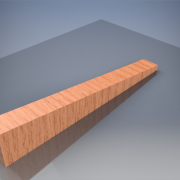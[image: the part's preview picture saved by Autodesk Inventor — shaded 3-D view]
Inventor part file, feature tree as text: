
AUTODESK INVENTOR PART (.ipt)
format: ipt  version: 2018 (Build 220112000, 112)  size: 120,320 bytes
history: native  units: in
note: dims shown in document units (in); Inventor stores cm internally (conversion verified against a paired STEP export)
features: extrude x1, sketch x1
ambient origin geometry x8: Origin, YZ Plane, XZ Plane, XY Plane, X Axis, Y Axis, Z Axis, Center Point
bodies: Solid1 (feature_tree)
feature tree (2):
  extrude  "Extrusion1"  Depth=7.5in
  sketch  "Sketch1"  dims[d0=1.25in d1=7.5in d2=0.25in d3=0.75in d4=0.0in]
